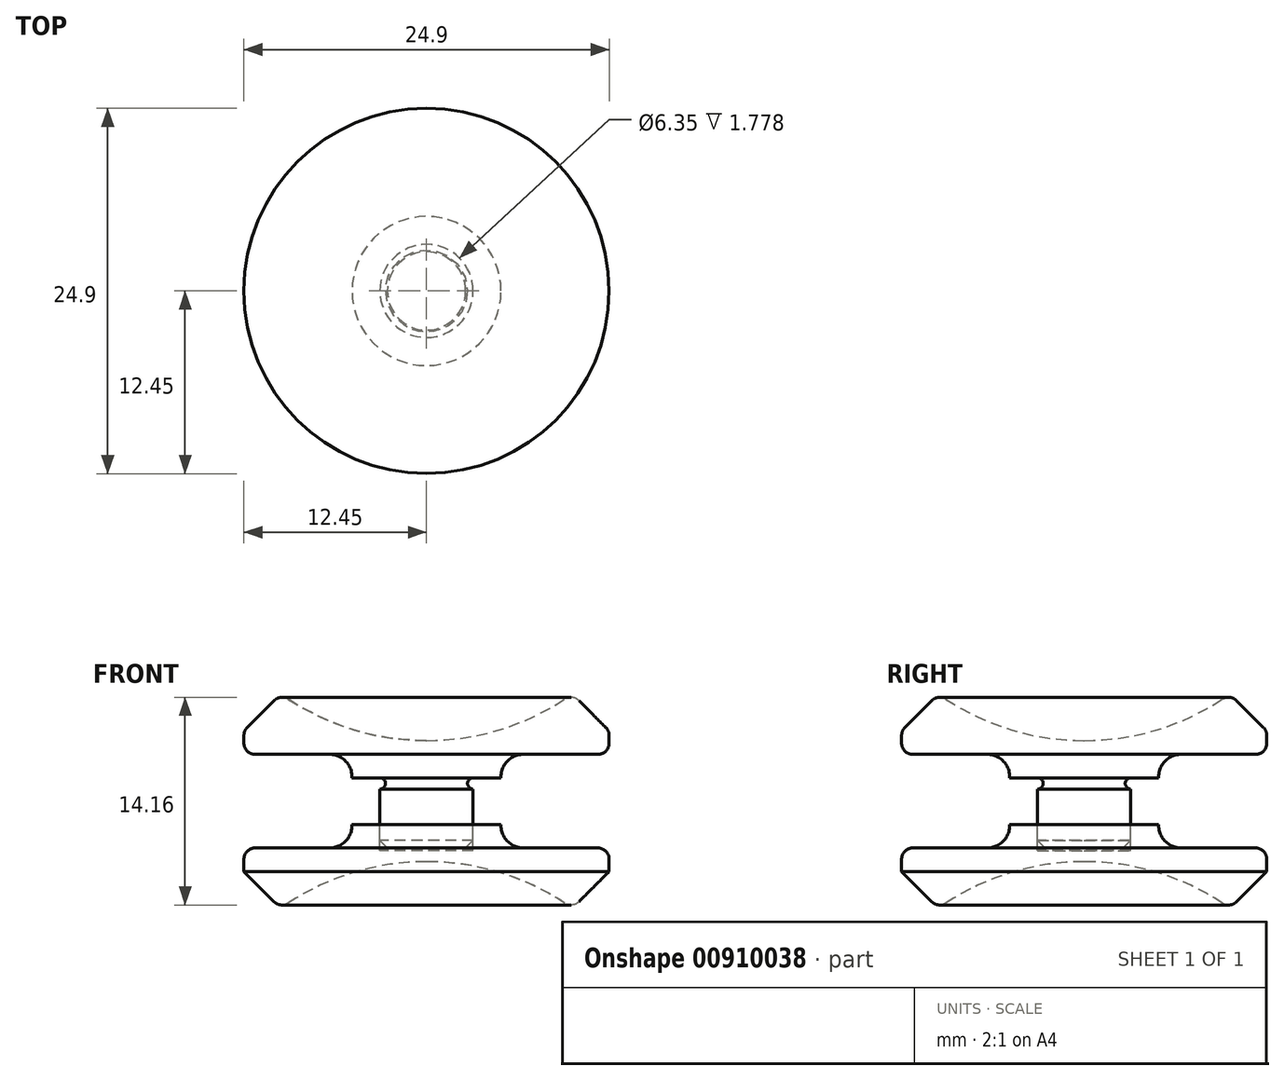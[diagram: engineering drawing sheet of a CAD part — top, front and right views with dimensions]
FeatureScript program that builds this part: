
annotation { "Feature Type Name" : "Feature", "Feature Type Description" : "" }
export const myFeature = defineFeature(function(context is Context, id is Id, definition is map)
    precondition{}
    {
        {
            var Q0;
            Q0=qCreatedBy(makeId("Front.planeOp"),FACE);
            var sketch = newSketch(context, id + "F0", { "sketchPlane" : qUnion([Q0])});
            skLineSegment(sketch, "E0", {"start": v(0, -4.76) * mm, "end": v(-3.17, -4.76) * mm});
            skLineSegment(sketch, "E1", {"start": v(-3.17, -4.76) * mm, "end": v(-3.17, 0) * mm});
            skLineSegment(sketch, "E2", {"start": v(-3.17, 0) * mm, "end": v(-5.08, 0) * mm});
            skLineSegment(sketch, "E3", {"start": v(-5.08, 0) * mm, "end": v(-5.08, 1.6) * mm});
            skLineSegment(sketch, "E4", {"start": v(-5.08, 1.6) * mm, "end": v(-12.45, 1.6) * mm});
            skLineSegment(sketch, "E5", {"start": v(-12.45, 1.6) * mm, "end": v(-12.45, 3.2) * mm});
            skLineSegment(sketch, "E6", {"start": v(-12.45, 3.2) * mm, "end": v(-9.94, 5.71) * mm});
            skArc(sketch, "E7", {"start": v(-9.94, 5.71) * mm, "mid": v(-5.22, 3.35) * mm, "end": v(0, 2.54) * mm});
            skLineSegment(sketch, "E8", {"start": v(0, 2.54) * mm, "end": v(0, -4.76) * mm});
            skCircle(sketch, "E9", {"center": v(-3.17, -0.38) * mm, "radius": 0.38 * mm});
            skSolve(sketch);
        }
        {
            var Q0;
            {var subQ2=sQuery(id+"F0.wireOp",EDGE,"E0");Q0=makeQuery(id+"F0.imprint","IMPRINT",FACE,{"disambiguationData":[TD([[makeQuery(id+"F0.imprint","IMPRINT",EDGE,{"derivedFrom":subQ2}),-1.0]])]});}
            var Q1;
            Q1=sQuery(id+"F0.wireOp",EDGE,"E8");
            revolve(context, id + "F1", {"surfaceOperationType" : NewSurfaceOperationType.NEW, "entities" : qUnion([Q0]), "axis" : qUnion([Q1]), "revolveType" : RevolveType.FULL});
        }
        {
            var Q0;
            Q0=makeQuery(id+"F1.opRevolve","SWEPT_EDGE",EDGE,{"disambiguationData":[OSD([sQuery(id+"F0.wireOp",EDGE,"E4"),sQuery(id+"F0.wireOp",EDGE,"E5")])]});
            fillet(context, id + "F2", {"entities" : qUnion([Q0]), "radius" : 0.76 * mm, "tangentPropagation" : true, "allowEdgeOverflow" : false});
        }
        {
            var Q0;
            Q0=makeQuery(id+"F1.opRevolve","SWEPT_EDGE",EDGE,{"disambiguationData":[OSD([sQuery(id+"F0.wireOp",EDGE,"E5"),sQuery(id+"F0.wireOp",EDGE,"E6")])]});
            var Q1;
            Q1=makeQuery(id+"F1.opRevolve","SWEPT_EDGE",EDGE,{"disambiguationData":[OSD([sQuery(id+"F0.wireOp",EDGE,"E6"),sQuery(id+"F0.wireOp",EDGE,"E7")])]});
            fillet(context, id + "F3", {"entities" : qUnion([Q0, Q1]), "radius" : 0.76 * mm, "tangentPropagation" : true, "allowEdgeOverflow" : false});
        }
        {
            var Q0;
            Q0=makeQuery(id+"F1.opRevolve","SWEPT_EDGE",EDGE,{"disambiguationData":[OSD([sQuery(id+"F0.wireOp",EDGE,"E0"),sQuery(id+"F0.wireOp",EDGE,"E1")])]});
            chamfer(context, id + "F4", {"entities" : qUnion([Q0]), "width" : 0.5 * mm, "tangentPropagation" : true});
        }
        {
            var Q0;
            Q0=makeQuery(id+"F1.opRevolve","SWEPT_EDGE",EDGE,{"disambiguationData":[OSD([sQuery(id+"F0.wireOp",EDGE,"E3"),sQuery(id+"F0.wireOp",EDGE,"E4")])]});
            fillet(context, id + "F5", {"entities" : qUnion([Q0]), "radius" : 1.52 * mm, "tangentPropagation" : true, "allowEdgeOverflow" : false});
        }
        {
            var Q0;
            Q0=qCreatedBy(makeId("Front.planeOp"),FACE);
            var sketch = newSketch(context, id + "F6", { "sketchPlane" : qUnion([Q0])});
            skLineSegment(sketch, "E10", {"start": v(-3.18, -3.17) * mm, "end": v(-5.08, -3.18) * mm});
            skLineSegment(sketch, "E11", {"start": v(-5.08, -3.18) * mm, "end": v(-5.08, -4.78) * mm});
            skLineSegment(sketch, "E12", {"start": v(-5.08, -4.78) * mm, "end": v(-12.45, -4.78) * mm});
            skLineSegment(sketch, "E13", {"start": v(-12.45, -4.78) * mm, "end": v(-12.45, -6.38) * mm});
            skLineSegment(sketch, "E14", {"start": v(-12.45, -6.38) * mm, "end": v(-9.94, -8.89) * mm});
            skArc(sketch, "E15", {"start": v(0, -5.71) * mm, "mid": v(-5.22, -6.53) * mm, "end": v(-9.94, -8.89) * mm});
            skLineSegment(sketch, "E16", {"start": v(0, -5.71) * mm, "end": v(0, -4.95) * mm});
            skLineSegment(sketch, "E17", {"start": v(-3.18, -3.18) * mm, "end": v(-3.18, -4.95) * mm});
            skLineSegment(sketch, "E18", {"start": v(-3.18, -4.95) * mm, "end": v(0, -4.95) * mm});
            skSolve(sketch);
        }
        {
            var Q0;
            Q0=makeQuery(id+"F6.imprint","IMPRINT",FACE,{"disambiguationData":[TD([[makeQuery(id+"F6.imprint","IMPRINT",EDGE,{"derivedFrom":sQuery(id+"F6.wireOp",EDGE,"E10")}),1.0]])]});
            var Q1;
            Q1=sQuery(id+"F0.wireOp",EDGE,"E8");
            revolve(context, id + "F7", {"surfaceOperationType" : NewSurfaceOperationType.NEW, "entities" : qUnion([Q0]), "axis" : qUnion([Q1]), "revolveType" : RevolveType.FULL});
        }
        {
            var Q0;
            Q0=makeQuery(id+"F7.opRevolve","SWEPT_EDGE",EDGE,{"disambiguationData":[OSD([sQuery(id+"F6.wireOp",EDGE,"E12"),sQuery(id+"F6.wireOp",EDGE,"E13")])]});
            var Q1;
            Q1=makeQuery(id+"F7.opRevolve","SWEPT_EDGE",EDGE,{"disambiguationData":[OSD([sQuery(id+"F6.wireOp",EDGE,"E14"),sQuery(id+"F6.wireOp",EDGE,"E15")])]});
            fillet(context, id + "F8", {"entities" : qUnion([Q0, Q1]), "radius" : 0.76 * mm, "tangentPropagation" : true, "allowEdgeOverflow" : false});
        }
        {
            var Q0;
            Q0=makeQuery(id+"F7.opRevolve","SWEPT_EDGE",EDGE,{"disambiguationData":[OSD([sQuery(id+"F6.wireOp",EDGE,"E11"),sQuery(id+"F6.wireOp",EDGE,"E12")])]});
            fillet(context, id + "F9", {"entities" : qUnion([Q0]), "radius" : 1.52 * mm, "tangentPropagation" : true, "allowEdgeOverflow" : false});
        }
    });
